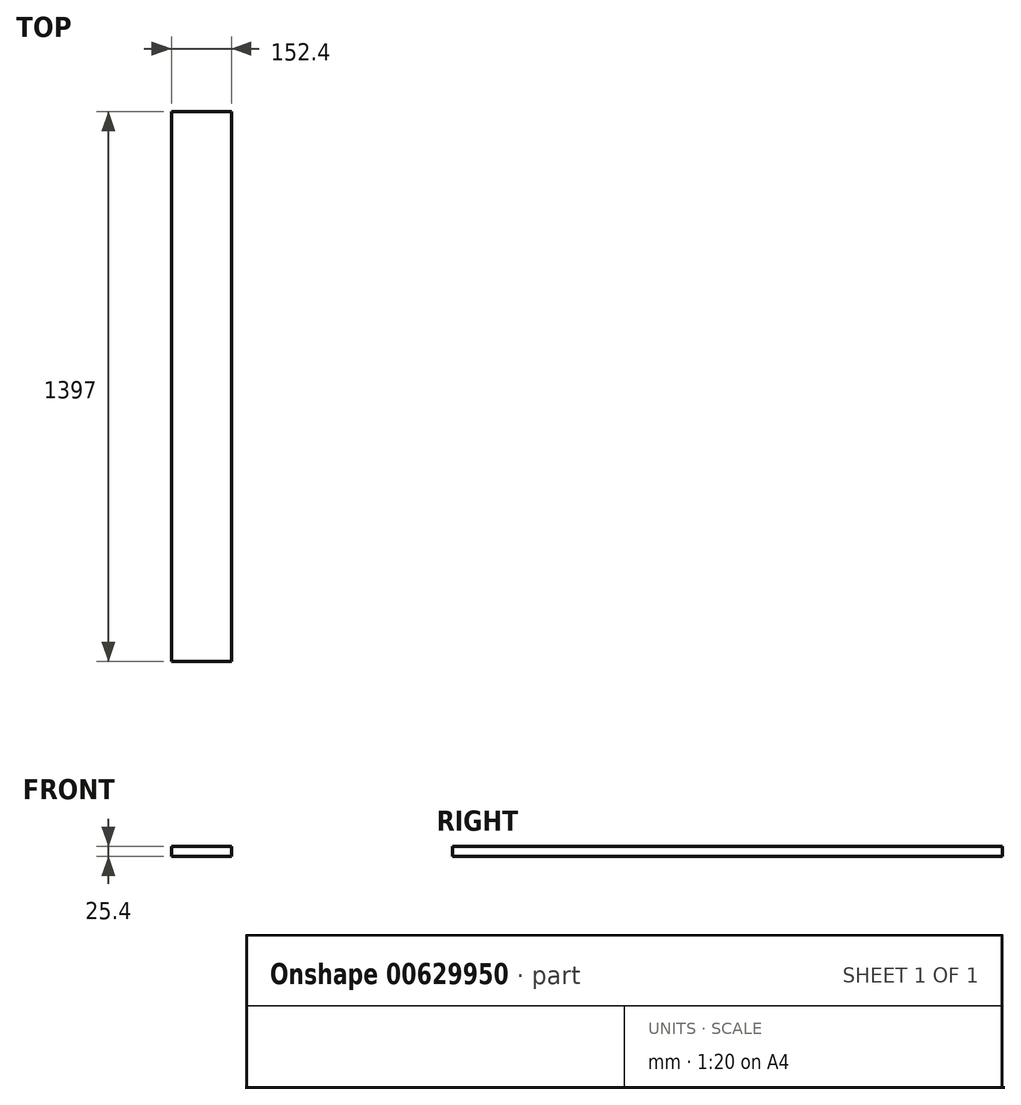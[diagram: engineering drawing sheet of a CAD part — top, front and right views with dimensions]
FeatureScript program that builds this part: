
annotation { "Feature Type Name" : "Feature", "Feature Type Description" : "" }
export const myFeature = defineFeature(function(context is Context, id is Id, definition is map)
    precondition{}
    {
        {
            var Q0;
            Q0=qCreatedBy(makeId("Front.planeOp"),FACE);
            var sketch = newSketch(context, id + "F0", { "sketchPlane" : qUnion([Q0])});
            skLineSegment(sketch, "E0.bottom", {"start": v(-67.25, 0.76) * mm, "end": v(85.15, 0.76) * mm});
            skLineSegment(sketch, "E0.top", {"start": v(-67.25, -24.64) * mm, "end": v(85.15, -24.64) * mm});
            skLineSegment(sketch, "E0.left", {"start": v(-67.25, 0.76) * mm, "end": v(-67.25, -24.64) * mm});
            skLineSegment(sketch, "E0.right", {"start": v(85.15, 0.76) * mm, "end": v(85.15, -24.64) * mm});
            skSolve(sketch);
        }
        {
            var Q0;
            Q0 = qSketchRegion(id + "F0", true);
            extrude(context, id + "F1", {"entities" : qUnion([Q0]), "depth" : 1397 * mm, "offsetDistance" : 25.4 * mm});
        }
    });
